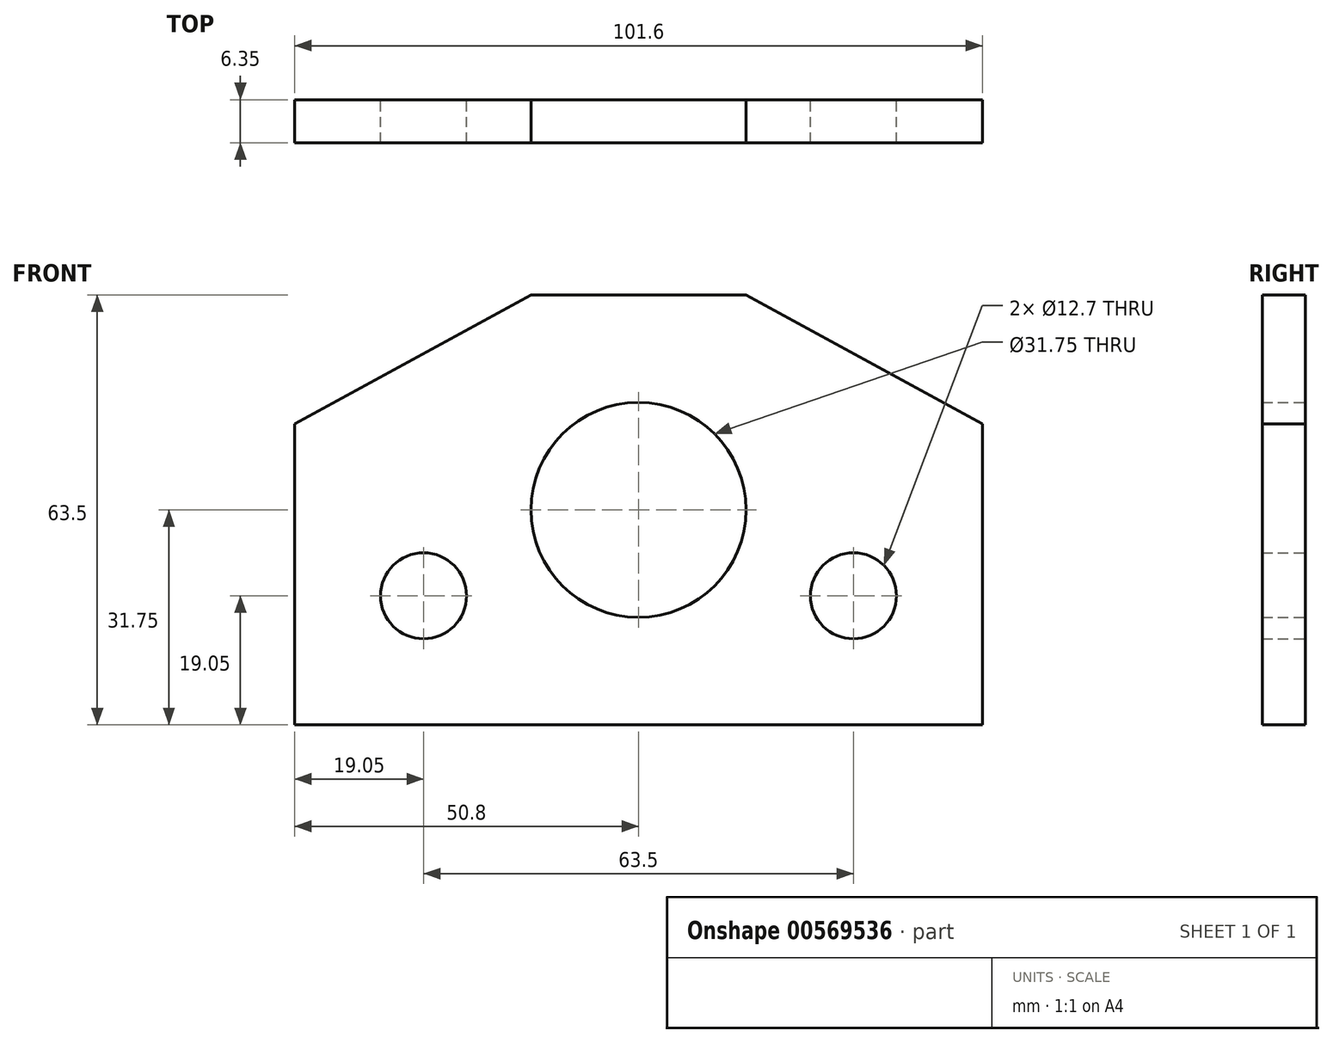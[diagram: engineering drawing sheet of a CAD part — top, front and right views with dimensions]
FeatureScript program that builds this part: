
annotation { "Feature Type Name" : "Feature", "Feature Type Description" : "" }
export const myFeature = defineFeature(function(context is Context, id is Id, definition is map)
    precondition{}
    {
        {
            var Q0;
            Q0=qCreatedBy(makeId("Front.planeOp"),FACE);
            var sketch = newSketch(context, id + "F0", { "sketchPlane" : qUnion([Q0])});
            skLineSegment(sketch, "E0.bottom", {"start": v(0, 0) * mm, "end": v(101.6, 0) * mm});
            skLineSegment(sketch, "E0.top", {"start": v(34.92, 63.5) * mm, "end": v(66.67, 63.5) * mm});
            skLineSegment(sketch, "E0.left", {"start": v(0, 0) * mm, "end": v(0, 44.45) * mm});
            skLineSegment(sketch, "E0.right", {"start": v(101.6, 0) * mm, "end": v(101.6, 44.45) * mm});
            skLineSegment(sketch, "E1.bottom", {"start": v(0, 0) * mm, "end": v(19.05, 0) * mm});
            skLineSegment(sketch, "E1.left", {"start": v(0, 0) * mm, "end": v(0, 19.05) * mm});
            skCircle(sketch, "E2", {"center": v(19.05, 19.05) * mm, "radius": 6.35 * mm});
            skLineSegment(sketch, "E3", {"start": v(50.8, 0) * mm, "end": v(50.8, 31.75) * mm});
            skCircle(sketch, "E4", {"center": v(50.8, 31.75) * mm, "radius": 15.88 * mm});
            skLineSegment(sketch, "E5", {"start": v(50.8, 63.5) * mm, "end": v(34.92, 63.5) * mm});
            skLineSegment(sketch, "E6", {"start": v(34.92, 63.5) * mm, "end": v(0, 44.45) * mm});
            skPoint(sketch, "E7.orphan", {"position": v(0, 63.5) * mm});
            skCircle(sketch, "E8.MirrorC", {"center": v(82.55, 19.05) * mm, "radius": 6.35 * mm});
            skLineSegment(sketch, "E9.MirrorCS", {"start": v(66.67, 63.5) * mm, "end": v(101.6, 44.45) * mm});
            skPoint(sketch, "E10.orphan", {"position": v(101.6, 63.5) * mm});
            skSolve(sketch);
        }
        {
            var Q0;
            Q0 = qSketchRegion(id + "F0", true);
            extrude(context, id + "F1", {"entities" : qUnion([Q0]), "depth" : 6.35 * mm, "offsetDistance" : 25.4 * mm});
        }
    });
